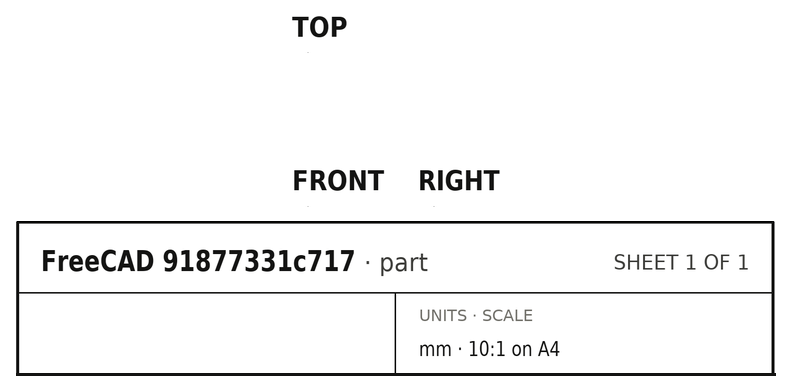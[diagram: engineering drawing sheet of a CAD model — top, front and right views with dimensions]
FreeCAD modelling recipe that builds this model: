
FCSTD DOCUMENT  (FreeCAD 0.21R33694 (Git))
Label: diffPair
License: All rights reserved
LicenseURL: http://en.wikipedia.org/wiki/All_rights_reserved
objects: Part::Part2DObjectPython×23, App::FeaturePython×10, Part::Extrusion×5, Part::Cut×3, Part::FeaturePython×2
note: 33 computed .brp shape members not serialized (recipe doc carries the construction recipe); baked Part::Feature solids carry a one-line shape summary decoded from their .brp

FEATURE [Part::Part2DObjectPython] Wire  # Draft 2D object (typed FeaturePython)
  Area = 0.0014181
  ChamferSize = 0
  Closed = true
  End = (-0.05,0,0)
  FilletRadius = 0
  Length = 0.221006
  MakeFace = true
  Placement = pos=(-0.15,0,0) rot=(0,0,1;0rad)
  Points = (4) [(0,0,0),(0.00545955,0.015,0),(0.0945402,0.015,0),(0.1,-6.12323e-18,0)]
  Start = (-0.15,0,0)
  Subdivisions = 0
FEATURE [Part::Part2DObjectPython] Wire001  # Draft 2D object (typed FeaturePython)
  Area = 0.0014181
  ChamferSize = 0
  Closed = true
  End = (0.15,0,0)
  FilletRadius = 0
  Length = 0.221006
  MakeFace = true
  Placement = pos=(0.05,0,0) rot=(0,0,1;0rad)
  Points = (4) [(0,0,0),(0.00545955,0.015,0),(0.0945402,0.015,0),(0.1,-6.12323e-18,0)]
  Start = (0.05,0,0)
  Subdivisions = 0
FEATURE [Part::Part2DObjectPython] Rectangle  # Draft 2D object (typed FeaturePython)
  Area = 0.13
  ChamferSize = 0
  Columns = 1
  FilletRadius = 0
  Height = 0.1
  Length = 1.3
  MakeFace = true
  Placement = pos=(-0.65,-0.1,0) rot=(0,0,1;0rad)
  Rows = 1
FEATURE [Part::Part2DObjectPython] Rectangle001  # Draft 2D object (typed FeaturePython)
  Area = 0.13
  ChamferSize = 0
  Columns = 1
  FilletRadius = 0
  Height = 0.1
  Length = 1.3
  MakeFace = true
  Placement = pos=(-0.65,0,0) rot=(0,0,1;0rad)
  Rows = 1
FEATURE [Part::Part2DObjectPython] Clone2D  label="Wire (2D)"  # Draft 2D object (typed FeaturePython)
  Fuse = false
  Objects = -> [Wire]
  Placement = pos=(-0.15,0,0) rot=(0,0,1;0rad)
  Scale = (1,1,1)
FEATURE [Part::Part2DObjectPython] Clone2D001  label="Wire001 (2D)"  # Draft 2D object (typed FeaturePython)
  Fuse = false
  Objects = -> [Wire001]
  Placement = pos=(0.05,0,0) rot=(0,0,1;0rad)
  Scale = (1,1,1)
FEATURE [Part::Part2DObjectPython] Clone2D002  label="Rectangle (2D)"  # Draft 2D object (typed FeaturePython)
  Fuse = false
  Objects = -> [Rectangle]
  Placement = pos=(-0.65,-0.1,0) rot=(0,0,1;0rad)
  Scale = (1,1,1)
FEATURE [Part::Part2DObjectPython] Clone2D003  label="Rectangle001 (2D)"  # Draft 2D object (typed FeaturePython)
  Fuse = false
  Objects = -> [Rectangle001]
  Placement = pos=(-0.65,0,0) rot=(0,0,1;0rad)
  Scale = (1,1,1)
FEATURE [Part::Part2DObjectPython] Clone2D004  label="Wire (2D)001"  # Draft 2D object (typed FeaturePython)
  Fuse = false
  Objects = -> [Wire]
  Placement = pos=(-0.15,0,0) rot=(0,0,1;0rad)
  Scale = (1,1,1)
FEATURE [Part::Part2DObjectPython] Clone2D005  label="Wire001 (2D)001"  # Draft 2D object (typed FeaturePython)
  Fuse = false
  Objects = -> [Wire001]
  Placement = pos=(0.05,0,0) rot=(0,0,1;0rad)
  Scale = (1,1,1)
FEATURE [Part::Part2DObjectPython] Clone2D006  label="Rectangle (2D)001"  # Draft 2D object (typed FeaturePython)
  Fuse = false
  Objects = -> [Rectangle]
  Placement = pos=(-0.65,-0.1,0) rot=(0,0,1;0rad)
  Scale = (1,1,1)
FEATURE [Part::Part2DObjectPython] Clone2D007  label="Rectangle001 (2D)001"  # Draft 2D object (typed FeaturePython)
  Fuse = false
  Objects = -> [Rectangle001]
  Placement = pos=(-0.65,0,0) rot=(0,0,1;0rad)
  Scale = (1,1,1)
FEATURE [Part::Extrusion] Extrude004
  Base = -> Clone2D
  Dir = (0,0,1)
  DirMode = 2
  FaceMakerClass = Part::FaceMakerBullseye
  LengthFwd = 2
  LengthRev = 0
  Solid = false
  Symmetric = false
FEATURE [Part::Extrusion] Extrude005
  Base = -> Clone2D001
  Dir = (0,0,1)
  DirMode = 2
  FaceMakerClass = Part::FaceMakerBullseye
  LengthFwd = 2
  LengthRev = 0
  Solid = false
  Symmetric = false
FEATURE [Part::Extrusion] Extrude006
  Base = -> Clone2D002
  Dir = (0,0,1)
  DirMode = 2
  FaceMakerClass = Part::FaceMakerBullseye
  LengthFwd = 2
  LengthRev = 0
  Solid = false
  Symmetric = false
FEATURE [Part::Extrusion] Extrude007
  Base = -> Clone2D003
  Dir = (0,0,1)
  DirMode = 2
  FaceMakerClass = Part::FaceMakerBullseye
  LengthFwd = 2
  LengthRev = 0
  Solid = false
  Symmetric = false
FEATURE [Part::Cut] Cut002
  Base = -> Extrude007
  Tool = -> Extrude004
FEATURE [Part::Cut] Cut003
  Base = -> Cut002
  Tool = -> Extrude005
FEATURE [App::FeaturePython] Text010  label="_Sin(PV){port1}"  # WARN: FeaturePython — macro-defined, semantics opaque (R4)
  Placement = pos=(5.00075,-5.09743,10) rot=(0,0,1;0rad)
  Text = .
FEATURE [App::FeaturePython] Text011  label="_Sout(PV){port2}"  # WARN: FeaturePython — macro-defined, semantics opaque (R4)
  Placement = pos=(5.00075,-5.09743,10) rot=(0,0,1;0rad)
  Text = .
FEATURE [App::FeaturePython] Text012  label="_Min(1,voltage,comm_in,0.5){v11,v12}"  # WARN: FeaturePython — macro-defined, semantics opaque (R4)
  Placement = pos=(5.00075,-5.09743,10) rot=(0,0,1;0rad)
  Text = .
FEATURE [App::FeaturePython] Text013  label="_Min(1,current,comm_in){i11,i12}"  # WARN: FeaturePython — macro-defined, semantics opaque (R4)
  Placement = pos=(5.00075,-5.09743,10) rot=(0,0,1;0rad)
  Text = .
FEATURE [App::FeaturePython] Text014  label="_Min(2,voltage,diff_in){v11,-v12}"  # WARN: FeaturePython — macro-defined, semantics opaque (R4)
  Placement = pos=(5.00075,-5.09743,10) rot=(0,0,1;0rad)
  Text = .
FEATURE [App::FeaturePython] Text015  label="_Min(2,current,diff_in,0.5){i11,-i12}"  # WARN: FeaturePython — macro-defined, semantics opaque (R4)
  Placement = pos=(5.00075,-5.09743,10) rot=(0,0,1;0rad)
  Text = .
FEATURE [App::FeaturePython] Text016  label="_Mout(3,voltage,comm_out,0.5){v21,v22}"  # WARN: FeaturePython — macro-defined, semantics opaque (R4)
  Placement = pos=(5.00075,-5.09743,10) rot=(0,0,1;0rad)
  Text = .
FEATURE [App::FeaturePython] Text017  label="_Mout(3,current,comm_out){i21,i22}"  # WARN: FeaturePython — macro-defined, semantics opaque (R4)
  Placement = pos=(5.00075,-5.09743,10) rot=(0,0,1;0rad)
  Text = .
FEATURE [App::FeaturePython] Text018  label="_Mout(4,voltage,diff_out){v21,-v22}"  # WARN: FeaturePython — macro-defined, semantics opaque (R4)
  Placement = pos=(5.00075,-5.09743,10) rot=(0,0,1;0rad)
  Text = .
FEATURE [App::FeaturePython] Text019  label="_Mout(4,current,diff_out,0.5){i21,-i22}"  # WARN: FeaturePython — macro-defined, semantics opaque (R4)
  Placement = pos=(5.00075,-5.09743,10) rot=(0,0,1;0rad)
  Text = .
FEATURE [Part::Part2DObjectPython] Wire006  label="_Pi22"  # Draft 2D object (typed FeaturePython)
  Area = 1.4181e-09
  ChamferSize = 0
  Closed = true
  End = (5e-05,-0.0999,4.995)
  FilletRadius = 0
  Length = 0.000221006
  MakeFace = true
  Placement = pos=(0.00015,-0.0999,4.995) rot=(0.707107,0.707107,0;3.14159rad)
  Points = (4) [(0,0,0),(1.5e-05,-5.45983e-06,0),(1.5e-05,-9.45404e-05,0),(0,-0.0001,0)]
  Start = (0.00015,-0.0999,4.995)
  Subdivisions = 0
FEATURE [Part::Part2DObjectPython] Wire007  label="_Pi21"  # Draft 2D object (typed FeaturePython)
  Area = 1.4181e-09
  ChamferSize = 0
  Closed = true
  End = (-0.00015,-0.0999,4.995)
  FilletRadius = 0
  Length = 0.000221006
  MakeFace = true
  Placement = pos=(-5e-05,-0.0999,4.995) rot=(0.707107,0.707107,0;3.14159rad)
  Points = (4) [(0,0,0),(1.5e-05,-5.45983e-06,0),(1.5e-05,-9.45404e-05,0),(0,-0.0001,0)]
  Start = (-5e-05,-0.0999,4.995)
  Subdivisions = 0
FEATURE [Part::Part2DObjectPython] Wire008  label="_Pi11"  # Draft 2D object (typed FeaturePython)
  Area = 1.4181e-09
  ChamferSize = 0
  Closed = true
  End = (-5e-05,-0.0999,4.997)
  FilletRadius = 0
  Length = 0.000221006
  MakeFace = true
  Placement = pos=(-0.00015,-0.0999,4.997) rot=(0,0,1;0rad)
  Points = (4) [(0,0,0),(5.45955e-06,1.5e-05,0),(9.45402e-05,1.5e-05,0),(0.0001,0,0)]
  Start = (-0.00015,-0.0999,4.997)
  Subdivisions = 0
FEATURE [Part::Part2DObjectPython] Wire009  label="_Pi12"  # Draft 2D object (typed FeaturePython)
  Area = 1.4181e-09
  ChamferSize = 0
  Closed = true
  End = (0.00015,-0.0999,4.997)
  FilletRadius = 0
  Length = 0.000221006
  MakeFace = true
  Placement = pos=(5e-05,-0.0999,4.997) rot=(0,0,1;0rad)
  Points = (4) [(0,0,0),(5.45955e-06,1.5e-05,0),(9.45402e-05,1.5e-05,0),(0.0001,0,0)]
  Start = (5e-05,-0.0999,4.997)
  Subdivisions = 0
FEATURE [Part::Part2DObjectPython] Rectangle013  label="_Pport1"  # Draft 2D object (typed FeaturePython)
  Area = 2.6e-07
  ChamferSize = 0
  Columns = 1
  FilletRadius = 0
  Height = 0.0002
  Length = 0.0013
  MakeFace = true
  Placement = pos=(-0.00065,-0.1,4.997) rot=(0,0,1;0rad)
  Rows = 1
FEATURE [Part::Part2DObjectPython] Line  label="_Pv11"  # Draft 2D object (typed FeaturePython)
  Area = 0
  ChamferSize = 0
  Closed = false
  End = (-0.0001,-0.0999,4.997)
  FilletRadius = 0
  Length = 0.0001
  MakeFace = true
  Placement = pos=(0,-0.1,4.997) rot=(0,0,1;0rad)
  Points = (2) [(-0.0001,0,0),(-0.0001,0.0001,0)]
  Start = (-0.0001,-0.1,4.997)
  Subdivisions = 0
FEATURE [Part::Part2DObjectPython] Line004  label="_Pv12"  # Draft 2D object (typed FeaturePython)
  Area = 0
  ChamferSize = 0
  Closed = false
  End = (0.0001,-0.0999,4.997)
  FilletRadius = 0
  Length = 0.0001
  MakeFace = true
  Placement = pos=(0,-0.1,4.997) rot=(0,0,1;0rad)
  Points = (2) [(0.0001,0,0),(0.0001,0.0001,0)]
  Start = (0.0001,-0.1,4.997)
  Subdivisions = 0
FEATURE [Part::Part2DObjectPython] Rectangle014  label="_Pport2"  # Draft 2D object (typed FeaturePython)
  Area = 2.6e-07
  ChamferSize = 0
  Columns = 1
  FilletRadius = 0
  Height = 0.0013
  Length = 0.0002
  MakeFace = true
  Placement = pos=(-0.00065,-0.1,4.995) rot=(0.707107,0.707107,0;3.14159rad)
  Rows = 1
FEATURE [Part::Part2DObjectPython] Line005  label="_Pv21"  # Draft 2D object (typed FeaturePython)
  Area = 0
  ChamferSize = 0
  Closed = false
  End = (-0.0001,-0.0999,4.995)
  FilletRadius = 0
  Length = 0.0001
  MakeFace = true
  Placement = pos=(0,-0.1,4.995) rot=(0.707107,0.707107,0;3.14159rad)
  Points = (2) [(1.38778e-17,-0.0001,0),(0.0001,-0.0001,0)]
  Start = (-0.0001,-0.1,4.995)
  Subdivisions = 0
FEATURE [Part::Part2DObjectPython] Line006  label="_Pv22"  # Draft 2D object (typed FeaturePython)
  Area = 0
  ChamferSize = 0
  Closed = false
  End = (0.0001,-0.0999,4.995)
  FilletRadius = 0
  Length = 0.0001
  MakeFace = true
  Placement = pos=(0,-0.1,4.995) rot=(0.707107,0.707107,0;3.14159rad)
  Points = (2) [(1.38778e-17,0.0001,0),(0.0001,0.0001,0)]
  Start = (0.0001,-0.1,4.995)
  Subdivisions = 0
FEATURE [Part::Part2DObjectPython] Rectangle015  # Draft 2D object (typed FeaturePython)
  Area = 0.01
  ChamferSize = 0
  Columns = 1
  FilletRadius = 0
  Height = 0.1
  Length = 0.1
  MakeFace = true
  Placement = pos=(-0.15,0,2.45) rot=(1,0,0;1.5708rad)
  Rows = 1
FEATURE [Part::Extrusion] Extrude
  Base = -> Rectangle015
  Dir = (0,-1,2e-16)
  DirMode = 2
  FaceMakerClass = Part::FaceMakerBullseye
  LengthFwd = 0.1
  LengthRev = 0
  Placement = pos=(0,0,-1.5) rot=(0,0,1;0rad)
  Solid = false
  Symmetric = false
FEATURE [Part::Cut] Cut
  Base = -> Extrude006
  Tool = -> Extrude
FEATURE [Part::FeaturePython] BooleanFragments  # WARN: FeaturePython — macro-defined, semantics opaque (R4)
  Mode = 0
  Objects = -> [Cut003,Cut]
  Tolerance = 0
FEATURE [Part::FeaturePython] Clone  label="scaled"  # Draft clone (typed FeaturePython)
  AttacherType = Attacher::AttachEngine3D
  Fuse = false
  Objects = -> [BooleanFragments]
  Placement = pos=(0,-0.0999,4.995) rot=(0,0,1;0rad)
  Scale = (0.001,0.001,0.001)
